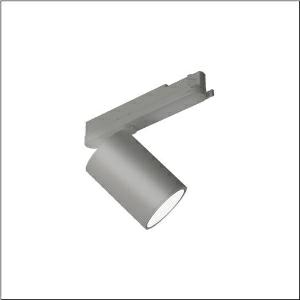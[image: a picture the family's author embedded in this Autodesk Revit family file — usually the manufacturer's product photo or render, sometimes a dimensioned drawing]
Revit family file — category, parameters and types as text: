
# Revit family: spot_31_51sf63mad4b
name_source: partatom
category: Lighting Fixtures
units: mm (PartAtom-declared; Revit-internal decimal feet)

## family parameters
Cut with Voids When Loaded = No
Host = Face
Light Source = No
Part Type = Normal
Room Calculation Point = No
Round Connector Dimension = Use Diameter
Shared = No

## types (1)
- --- (1 x LED, 5190 lm, 41.5 W, 4000K)
    Apparent Load = 42 VA
    CIE Flux Codes = 92 97 99 100 100
    Color Rendering = 90
    Color Temperature = 4000K
    Default Elevation = 1800 mm
    Description = Spot 31, directional spotlight, light control with lens, of PMMA, LED rated luminous flux: 4.980lm, light colour: 940, with 3-phase adapter, mains connection: 220..240V, AC, 50/60Hz, of aluminium, metallic grey (RAL 9006), length: 213mm, diameter: 90mm, protection rating (complete): IP20, insulation class (complete): insulation class I (protective earthing), certification: CE, impact resistance: IK02, permissible ambient temperature for indoor applications: -20..+40°C, packaging unit: 1 piece
    Height = 175 mm
    Lamp = 1 x LED
    Lamp Light Flux = 5190 lm
    Lamp Power = 41.5 W
    Lamp count = 1
    Length = 90 mm
    Luminous efficacy = 125 lm/W
    Manufacturer = Siteco
    ModVariant = No
    Model = 51SF63MAD4B
    Mounting Place = Ceiling
    Mounting Type = Pendant
    Number of Poles = 1
    OnlyDefault = Yes
    Power Factor = 1
    Product Name = Spot 31
    Product group = directional spotlight
    ProductGroupID = 905
    Protection Class = Protection class I
    Protection Degree = IP 20
    RLX_Detail_Level = 1
    RLX_Emergency_Light_Flux = 0 lm
    RLX_Emergency_Type = 0
    RLX_Emergency_Type_DB = No
    RlxData = <blob elided: 19941 chars, md5=c4e16dd0>
    Socket = socket
    Standby Power = 0 W
    System Light Flux = 5190 lm
    System Power = 42 W
    Type Comments = factory setting: luminous flux: 100 % | (ON | ON | ON | ON) | 1050 mA
    Type Image = l_1273725.jpg
    URL = http://relux.com
    VarID = @adj_078281
    Voltage = 0 V
    Weight = 0.00 kg
    Width = 0 mm  [stored 0 ft]

note: [stored X ft] marks values corroborated as IEEE doubles in the binary element streams (Revit-internal decimal feet)

## geometry (parser evidence)
native form markers: Blend x4, Sweep x9
no freeform markers — native parametric forms only
